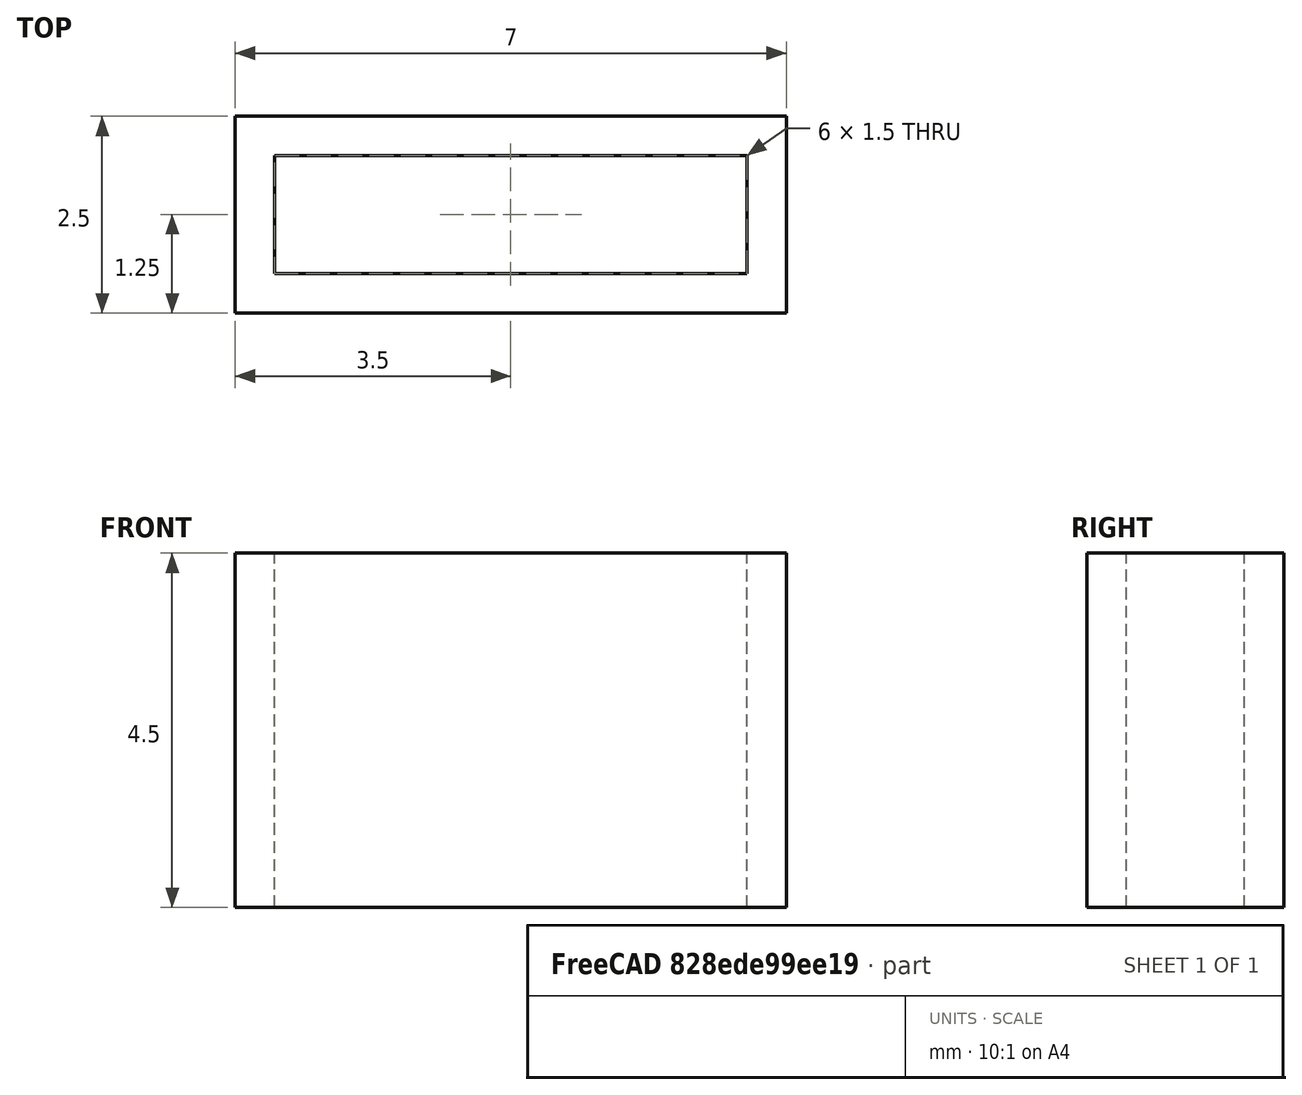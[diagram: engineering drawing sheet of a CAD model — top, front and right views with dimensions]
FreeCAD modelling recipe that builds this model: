
FCSTD DOCUMENT  (FreeCAD 0.18.4R)
Label: joint-protector
License: All rights reserved
LicenseURL: http://en.wikipedia.org/wiki/All_rights_reserved
objects: Sketcher::SketchObject×1, PartDesign::Pad×1, PartDesign::Body×1
note: 4 computed .brp shape members not serialized (recipe doc carries the construction recipe); baked Part::Feature solids carry a one-line shape summary decoded from their .brp

FEATURE [Sketcher::SketchObject] Sketch
  MapMode = 5
  Support = -> [XY_Plane]
  sketch-geometry (10):
    g0: LineSegment StartX=-3 StartY=0.75 StartZ=0 EndX=3 EndY=0.75 EndZ=0
    g1: LineSegment StartX=3 StartY=0.75 StartZ=0 EndX=3 EndY=-0.75 EndZ=0
    g2: LineSegment StartX=3 StartY=-0.75 StartZ=0 EndX=-3 EndY=-0.75 EndZ=0
    g3: LineSegment StartX=-3 StartY=-0.75 StartZ=0 EndX=-3 EndY=0.75 EndZ=0
    g4: LineSegment StartX=-3.5 StartY=1.25 StartZ=0 EndX=3.5 EndY=1.25 EndZ=0
    g5: LineSegment StartX=3.5 StartY=1.25 StartZ=0 EndX=3.5 EndY=-1.25 EndZ=0
    g6: LineSegment StartX=3.5 StartY=-1.25 StartZ=0 EndX=-3.5 EndY=-1.25 EndZ=0
    g7: LineSegment StartX=-3.5 StartY=-1.25 StartZ=0 EndX=-3.5 EndY=1.25 EndZ=0
    g8: LineSegment [constr] StartX=-3.5 StartY=0.75 StartZ=0 EndX=-3 EndY=0.75 EndZ=0
    g9: LineSegment [constr] StartX=-3 StartY=0.75 StartZ=0 EndX=-3 EndY=1.25 EndZ=0
  constraints (26):
    c: Coincident(g0,g1)
    c: Coincident(g1,g2)
    c: Coincident(g2,g3)
    c: Coincident(g3,g0)
    c: Horizontal(g2)
    c: Vertical(g1)
    c: Coincident(g4,g5)
    c: Coincident(g5,g6)
    c: Coincident(g6,g7)
    c: Coincident(g7,g4)
    c: Horizontal(g6)
    c: Vertical(g5)
    c: Symmetric(g0,g0,g-2)
    c: Symmetric(g0,g2,g-1)
    c: Symmetric(g6,g4,g-1)
    c: Symmetric(g4,g4,g-2)
    c: DistanceX(g0,g0) = 6
    c: DistanceY(g1,g1) = 1.5
    c: PointOnObject(g8,g7)
    c: Coincident(g8,g0)
    c: Horizontal(g8)
    c: Coincident(g8,g9)
    c: PointOnObject(g9,g4)
    c: Vertical(g9)
    c: Equal(g9,g8)
    c: Distance(g8) = 0.5
FEATURE [PartDesign::Pad] Pad
  Length = 4.5
  Length2 = 100
  Profile = -> Sketch
  Type = 0
FEATURE [PartDesign::Body] Body
  Group = -> [Sketch,Pad]
  Origin = -> Origin
  Tip = -> Pad
